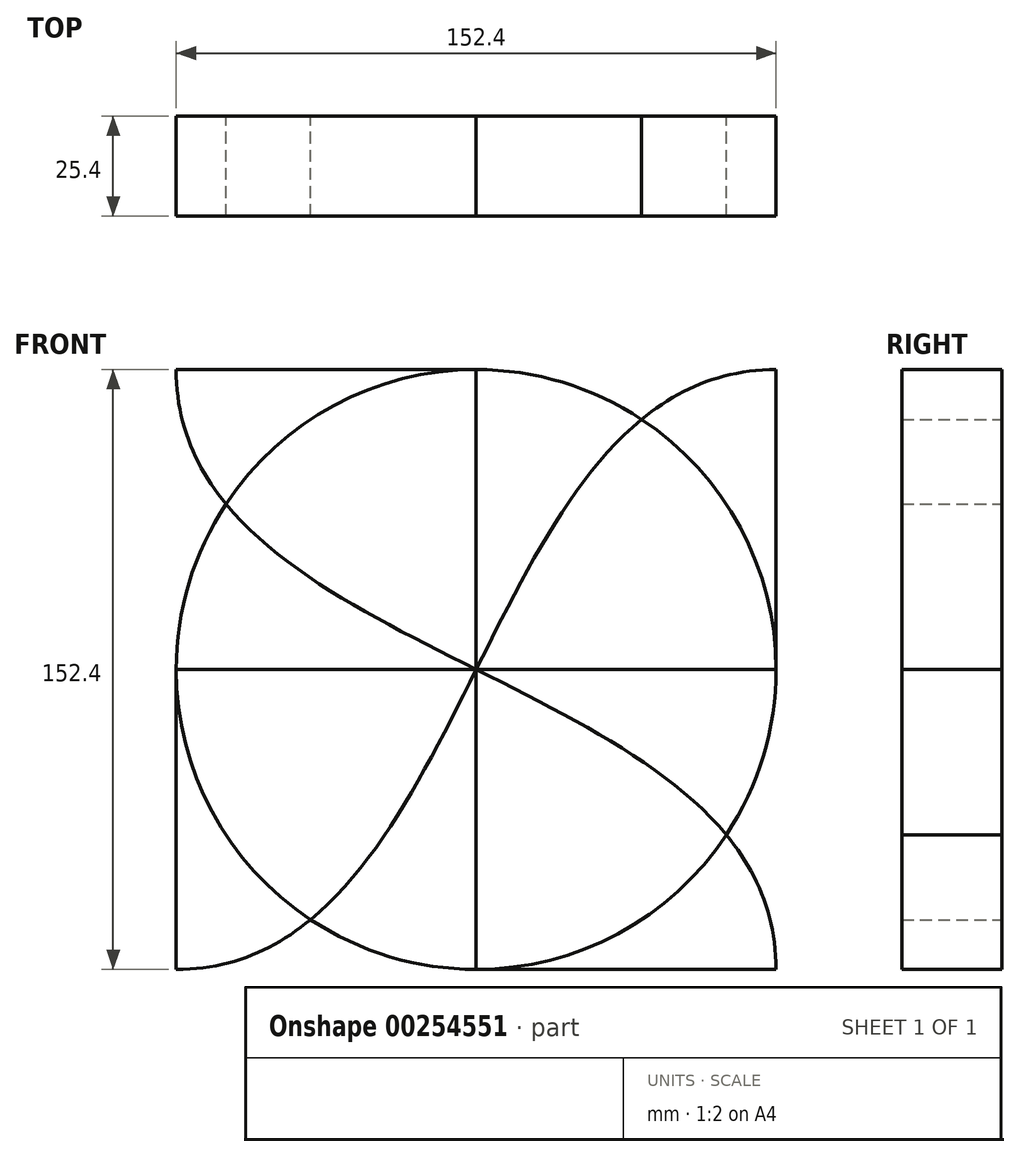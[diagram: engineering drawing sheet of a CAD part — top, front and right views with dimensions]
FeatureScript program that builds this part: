
annotation { "Feature Type Name" : "Feature", "Feature Type Description" : "" }
export const myFeature = defineFeature(function(context is Context, id is Id, definition is map)
    precondition{}
    {
        {
            var Q0;
            Q0=qCreatedBy(makeId("Front.planeOp"),FACE);
            var sketch = newSketch(context, id + "F0", { "sketchPlane" : qUnion([Q0])});
            skLineSegment(sketch, "E0.bottom", {"start": v(-76.2, -76.2) * mm, "end": v(76.2, -76.2) * mm});
            skLineSegment(sketch, "E0.top", {"start": v(-76.2, 76.2) * mm, "end": v(76.2, 76.2) * mm});
            skLineSegment(sketch, "E0.left", {"start": v(-76.2, -76.2) * mm, "end": v(-76.2, 76.2) * mm});
            skLineSegment(sketch, "E0.right", {"start": v(76.2, -76.2) * mm, "end": v(76.2, 76.2) * mm});
            skPoint(sketch, "E0.middle", {"position": v(0, 0) * mm});
            skFitSpline(sketch, "E1", {"points": [v(-76.2, -76.2) * mm, v(76.2, 76.2) * mm], "startDerivative": vector(228.6, 0) * mm, "endDerivative": vector(228.6, 0) * mm});
            skFitSpline(sketch, "E2", {"points": [v(-76.2, 76.2) * mm, v(76.2, -76.2) * mm], "startDerivative": vector(0, -228.6) * mm, "endDerivative": vector(0, -228.6) * mm});
            skCircle(sketch, "E3", {"center": v(0, 0) * mm, "radius": 76.2 * mm});
            skLineSegment(sketch, "E4", {"start": v(-76.2, 0) * mm, "end": v(76.2, 0) * mm});
            skLineSegment(sketch, "E5", {"start": v(0, 76.2) * mm, "end": v(0, -76.2) * mm});
            skSolve(sketch);
        }
        {
            var Q0;
            {var subQ0=sQuery(id+"F0.wireOp",EDGE,"E2");var subQ3=sQuery(id+"F0.wireOp",EDGE,"E3");var subQ5=makeQuery(id+"F0.imprint","INTERSECT",VERTEX,{"disambiguationData":[OD(1.0)],"derivedFrom":[subQ0,subQ3]});Q0=makeQuery(id+"F0.imprint","IMPRINT",FACE,{"disambiguationData":[TD([[makeQuery(id+"F0.imprint","IMPRINT",EDGE,{"disambiguationData":[TD([[subQ5,-1.0]])],"derivedFrom":subQ0}),-1.0]])]});}
            var Q1;
            {var subQ0=sQuery(id+"F0.wireOp",EDGE,"E2");var subQ3=sQuery(id+"F0.wireOp",EDGE,"E3");var subQ5=makeQuery(id+"F0.imprint","INTERSECT",VERTEX,{"disambiguationData":[OD(0.0)],"derivedFrom":[subQ0,subQ3]});Q1=makeQuery(id+"F0.imprint","IMPRINT",FACE,{"disambiguationData":[TD([[makeQuery(id+"F0.imprint","IMPRINT",EDGE,{"disambiguationData":[TD([[subQ5,1.0]])],"derivedFrom":subQ0}),1.0]])]});}
            var Q2;
            {var subQ0=sQuery(id+"F0.wireOp",EDGE,"E1");var subQ3=sQuery(id+"F0.wireOp",EDGE,"E3");var subQ5=makeQuery(id+"F0.imprint","INTERSECT",VERTEX,{"disambiguationData":[OD(0.0)],"derivedFrom":[subQ0,subQ3]});Q2=makeQuery(id+"F0.imprint","IMPRINT",FACE,{"disambiguationData":[TD([[makeQuery(id+"F0.imprint","IMPRINT",EDGE,{"disambiguationData":[TD([[subQ5,1.0]])],"derivedFrom":subQ0}),1.0]])]});}
            var Q3;
            {var subQ0=sQuery(id+"F0.wireOp",EDGE,"E1");var subQ3=sQuery(id+"F0.wireOp",EDGE,"E3");var subQ5=makeQuery(id+"F0.imprint","INTERSECT",VERTEX,{"disambiguationData":[OD(1.0)],"derivedFrom":[subQ0,subQ3]});Q3=makeQuery(id+"F0.imprint","IMPRINT",FACE,{"disambiguationData":[TD([[makeQuery(id+"F0.imprint","IMPRINT",EDGE,{"disambiguationData":[TD([[subQ5,-1.0]])],"derivedFrom":subQ0}),-1.0]])]});}
            var Q4;
            {var subQ0=sQuery(id+"F0.wireOp",EDGE,"E3");var subQ1=sQuery(id+"F0.wireOp",EDGE,"E1");var subQ2=makeQuery(id+"F0.imprint","INTERSECT",VERTEX,{"disambiguationData":[OD(0.0)],"derivedFrom":[subQ1,subQ0]});Q4=makeQuery(id+"F0.imprint","IMPRINT",FACE,{"disambiguationData":[TD([[makeQuery(id+"F0.imprint","IMPRINT",EDGE,{"disambiguationData":[TD([[subQ2,-1.0]])],"derivedFrom":subQ0}),1.0]])]});}
            var Q5;
            {var subQ0=sQuery(id+"F0.wireOp",EDGE,"E3");var subQ1=sQuery(id+"F0.wireOp",EDGE,"E1");var subQ2=makeQuery(id+"F0.imprint","INTERSECT",VERTEX,{"disambiguationData":[OD(1.0)],"derivedFrom":[subQ1,subQ0]});Q5=makeQuery(id+"F0.imprint","IMPRINT",FACE,{"disambiguationData":[TD([[makeQuery(id+"F0.imprint","IMPRINT",EDGE,{"disambiguationData":[TD([[subQ2,-1.0]])],"derivedFrom":subQ0}),1.0]])]});}
            var Q6;
            {var subQ0=sQuery(id+"F0.wireOp",EDGE,"E3");var subQ1=sQuery(id+"F0.wireOp",EDGE,"E2");var subQ2=makeQuery(id+"F0.imprint","INTERSECT",VERTEX,{"disambiguationData":[OD(0.0)],"derivedFrom":[subQ1,subQ0]});Q6=makeQuery(id+"F0.imprint","IMPRINT",FACE,{"disambiguationData":[TD([[makeQuery(id+"F0.imprint","IMPRINT",EDGE,{"disambiguationData":[TD([[subQ2,-1.0]])],"derivedFrom":subQ0}),1.0]])]});}
            var Q7;
            {var subQ0=sQuery(id+"F0.wireOp",EDGE,"E3");var subQ1=sQuery(id+"F0.wireOp",EDGE,"E2");var subQ2=makeQuery(id+"F0.imprint","INTERSECT",VERTEX,{"disambiguationData":[OD(1.0)],"derivedFrom":[subQ1,subQ0]});Q7=makeQuery(id+"F0.imprint","IMPRINT",FACE,{"disambiguationData":[TD([[makeQuery(id+"F0.imprint","IMPRINT",EDGE,{"disambiguationData":[TD([[subQ2,-1.0]])],"derivedFrom":subQ0}),1.0]])]});}
            extrude(context, id + "F1", {"entities" : qUnion([Q0, Q1, Q2, Q3, Q4, Q5, Q6, Q7]), "depth" : 25.4 * mm});
        }
    });
